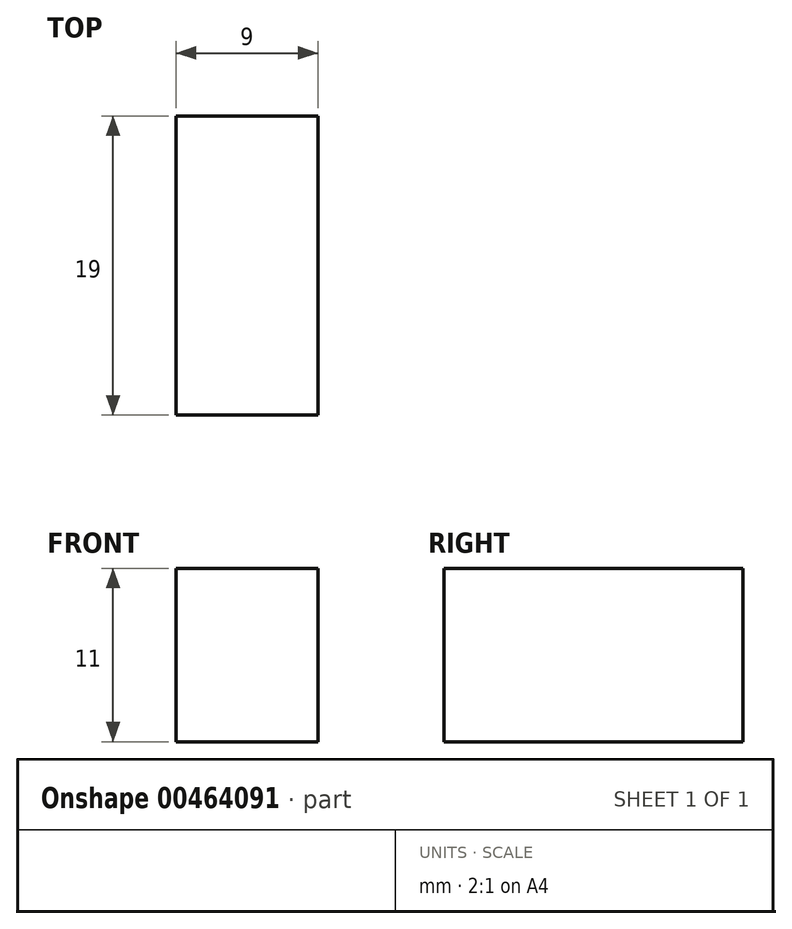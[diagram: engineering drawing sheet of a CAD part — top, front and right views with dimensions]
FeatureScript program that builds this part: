
annotation { "Feature Type Name" : "Feature", "Feature Type Description" : "" }
export const myFeature = defineFeature(function(context is Context, id is Id, definition is map)
    precondition{}
    {
        {
            var Q0;
            Q0=qCreatedBy(makeId("Top.planeOp"),FACE);
            var sketch = newSketch(context, id + "F0", { "sketchPlane" : qUnion([Q0])});
            skLineSegment(sketch, "E0.bottom", {"start": v(-7.8, 14.98) * mm, "end": v(1.2, 14.98) * mm});
            skLineSegment(sketch, "E0.top", {"start": v(-7.8, -4.02) * mm, "end": v(1.2, -4.02) * mm});
            skLineSegment(sketch, "E0.left", {"start": v(-7.8, 14.98) * mm, "end": v(-7.8, -4.02) * mm});
            skLineSegment(sketch, "E0.right", {"start": v(1.2, 14.98) * mm, "end": v(1.2, -4.02) * mm});
            skSolve(sketch);
        }
        {
            var Q0;
            Q0=makeQuery(id+"F0.imprint","IMPRINT",FACE,{"disambiguationData":[TD([[makeQuery(id+"F0.imprint","IMPRINT",EDGE,{"derivedFrom":sQuery(id+"F0.wireOp",EDGE,"E0.bottom")}),-1.0]])]});
            extrude(context, id + "F1", {"entities" : qUnion([Q0]), "depth" : 11 * mm});
        }
    });
